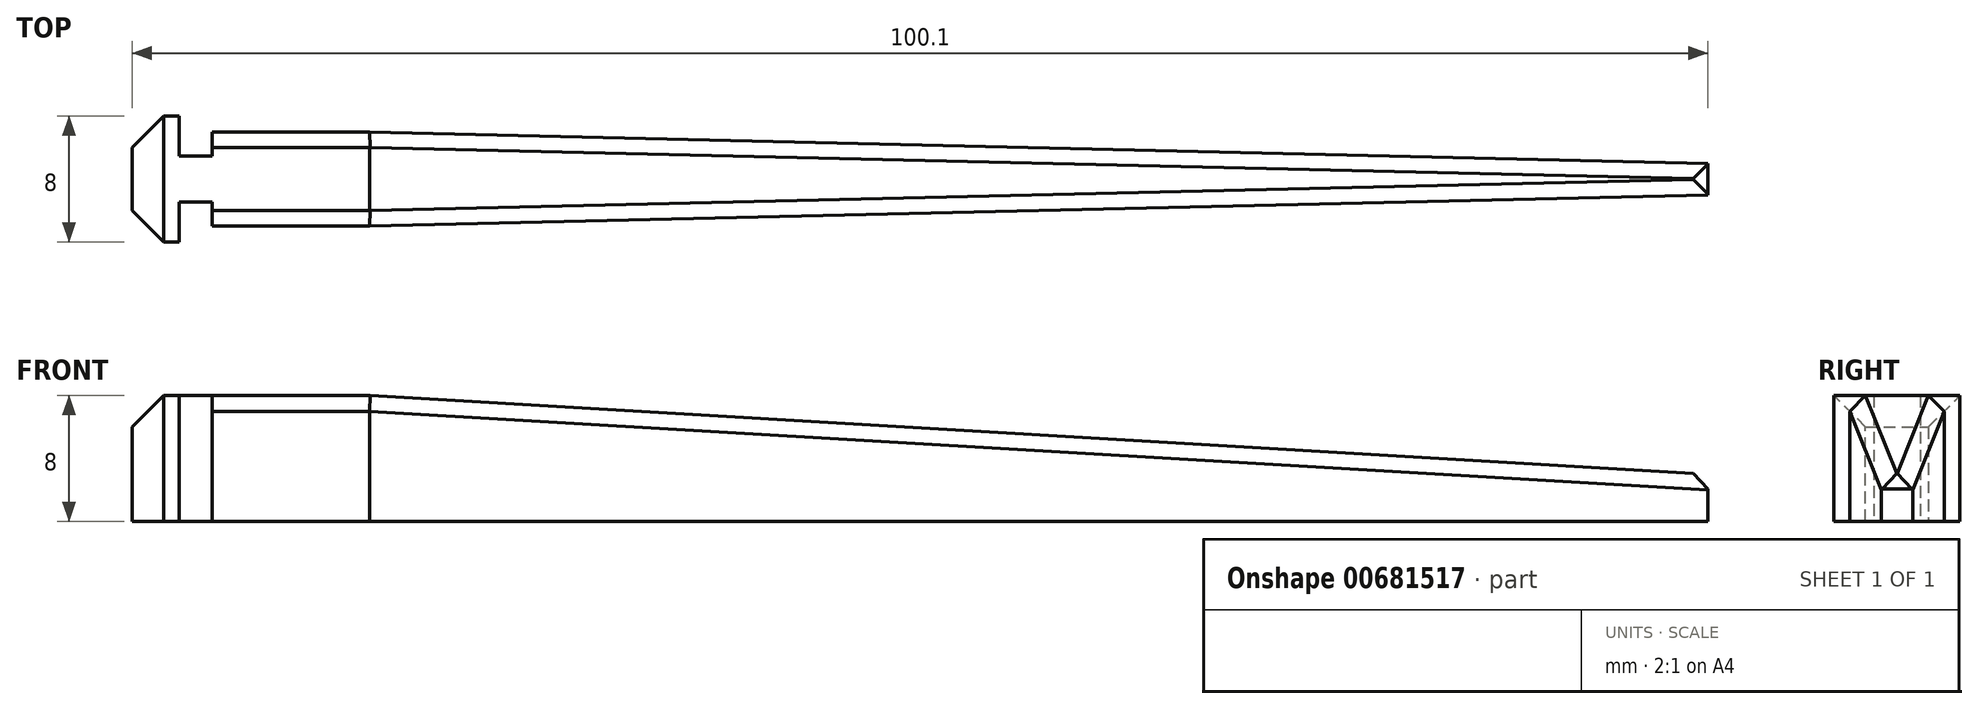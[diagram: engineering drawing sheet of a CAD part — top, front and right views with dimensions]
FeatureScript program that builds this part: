
annotation { "Feature Type Name" : "Feature", "Feature Type Description" : "" }
export const myFeature = defineFeature(function(context is Context, id is Id, definition is map)
    precondition{}
    {
        {
            var Q0;
            Q0=qCreatedBy(makeId("Top.planeOp"),FACE);
            var sketch = newSketch(context, id + "F0", { "sketchPlane" : qUnion([Q0])});
            skLineSegment(sketch, "E0.bottom", {"start": v(0, 0) * mm, "end": v(95, 0) * mm});
            skLineSegment(sketch, "E0.top", {"start": v(0, 6) * mm, "end": v(95, 6) * mm});
            skLineSegment(sketch, "E0.left", {"start": v(0, 0) * mm, "end": v(0, 1.52) * mm});
            skLineSegment(sketch, "E0.right", {"start": v(95, 0) * mm, "end": v(95, 6) * mm});
            skLineSegment(sketch, "E1.bottom", {"start": v(-2.1, 4.47) * mm, "end": v(0, 4.47) * mm});
            skLineSegment(sketch, "E1.top", {"start": v(-2.1, 1.52) * mm, "end": v(0, 1.52) * mm});
            skLineSegment(sketch, "E2.trimOffspring", {"start": v(0, 4.47) * mm, "end": v(0, 6) * mm});
            skLineSegment(sketch, "E3.bottom", {"start": v(-2.1, -1) * mm, "end": v(-5.1, -1) * mm});
            skLineSegment(sketch, "E3.top", {"start": v(-2.1, 7) * mm, "end": v(-5.1, 7) * mm});
            skLineSegment(sketch, "E3.left", {"start": v(-2.1, -1) * mm, "end": v(-2.1, 1.52) * mm});
            skLineSegment(sketch, "E3.right", {"start": v(-5.1, -1) * mm, "end": v(-5.1, 7) * mm});
            skLineSegment(sketch, "E4.trimOffspring", {"start": v(-2.1, 4.47) * mm, "end": v(-2.1, 7) * mm});
            skSolve(sketch);
        }
        {
            var Q0;
            Q0=makeQuery(id+"F0.imprint","IMPRINT",FACE,{"disambiguationData":[TD([[makeQuery(id+"F0.imprint","IMPRINT",EDGE,{"derivedFrom":sQuery(id+"F0.wireOp",EDGE,"E0.bottom")}),1.0]])]});
            extrude(context, id + "F1", {"entities" : qUnion([Q0]), "depth" : 8 * mm, "offsetDistance" : 25 * mm});
        }
        {
            var Q0;
            Q0=makeQuery(id+"F1.opExtrude","SWEPT_EDGE",EDGE,{"disambiguationData":[OSD([sQuery(id+"F0.wireOp",EDGE,"E3.top"),sQuery(id+"F0.wireOp",EDGE,"E3.right")])]});
            var Q1;
            Q1=makeQuery(id+"F1.opExtrude","CAP_EDGE",EDGE,{"disambiguationData":[OSD([sQuery(id+"F0.wireOp",EDGE,"E3.right")])],"isStart":false});
            var Q2;
            Q2=makeQuery(id+"F1.opExtrude","SWEPT_EDGE",EDGE,{"disambiguationData":[OSD([sQuery(id+"F0.wireOp",EDGE,"E3.bottom"),sQuery(id+"F0.wireOp",EDGE,"E3.right")])]});
            chamfer(context, id + "F2", {"entities" : qUnion([Q0, Q1, Q2]), "width" : 2 * mm, "tangentPropagation" : true});
        }
        {
            var Q0;
            Q0=makeQuery(id+"F1.opExtrude","CAP_EDGE",EDGE,{"disambiguationData":[OSD([sQuery(id+"F0.wireOp",EDGE,"E0.right")])],"isStart":false});
            chamfer(context, id + "F3", {"entities" : qUnion([Q0]), "chamferType" : ChamferType.TWO_OFFSETS, "width1" : 85 * mm, "oppositeDirection" : false, "width2" : 5 * mm, "tangentPropagation" : true});
        }
        {
            var Q0;
            Q0=makeQuery(id+"F1.opExtrude","SWEPT_EDGE",EDGE,{"disambiguationData":[OSD([sQuery(id+"F0.wireOp",EDGE,"E0.bottom"),sQuery(id+"F0.wireOp",EDGE,"E0.right")])]});
            var Q1;
            Q1=makeQuery(id+"F1.opExtrude","SWEPT_EDGE",EDGE,{"disambiguationData":[OSD([sQuery(id+"F0.wireOp",EDGE,"E0.top"),sQuery(id+"F0.wireOp",EDGE,"E0.right")])]});
            chamfer(context, id + "F4", {"entities" : qUnion([Q0, Q1]), "chamferType" : ChamferType.TWO_OFFSETS, "width1" : 2 * mm, "oppositeDirection" : false, "width2" : 85 * mm, "tangentPropagation" : true});
        }
        {
            var Q0;
            {var subQ0=sQuery(id+"F0.wireOp",EDGE,"E0.right");Q0=makeQuery(id+"F4.opChamfer","BLEND_EDGE",EDGE,{"blendedFrom":[makeQuery(id+"F1.opExtrude","SWEPT_EDGE",EDGE,{"disambiguationData":[OSD([sQuery(id+"F0.wireOp",EDGE,"E0.bottom"),subQ0])]}),makeQuery(id+"F3.opChamfer","BLEND_FACE",FACE,{"disambiguationData":[OSD([subQ0])]})],"blendedInto":[makeQuery(id+"F3.opChamfer","BLEND_FACE",FACE,{"disambiguationData":[OSD([subQ0])]})]});}
            var Q1;
            {var subQ0=sQuery(id+"F0.wireOp",EDGE,"E0.right");Q1=makeQuery(id+"F4.opChamfer","BLEND_EDGE",EDGE,{"blendedFrom":[makeQuery(id+"F1.opExtrude","SWEPT_EDGE",EDGE,{"disambiguationData":[OSD([sQuery(id+"F0.wireOp",EDGE,"E0.top"),subQ0])]}),makeQuery(id+"F3.opChamfer","BLEND_FACE",FACE,{"disambiguationData":[OSD([subQ0])]})],"blendedInto":[makeQuery(id+"F3.opChamfer","BLEND_FACE",FACE,{"disambiguationData":[OSD([subQ0])]})]});}
            var Q2;
            Q2=makeQuery(id+"F1.opExtrude","CAP_EDGE",EDGE,{"disambiguationData":[OSD([sQuery(id+"F0.wireOp",EDGE,"E0.bottom")])],"isStart":false});
            var Q3;
            Q3=makeQuery(id+"F1.opExtrude","CAP_EDGE",EDGE,{"disambiguationData":[OSD([sQuery(id+"F0.wireOp",EDGE,"E0.top")])],"isStart":false});
            var Q4;
            {var subQ0=sQuery(id+"F0.wireOp",EDGE,"E0.right");Q4=makeQuery(id+"F3.opChamfer","BLEND_EDGE",EDGE,{"blendedFrom":[makeQuery(id+"F1.opExtrude","CAP_EDGE",EDGE,{"disambiguationData":[OSD([subQ0])],"isStart":false}),makeQuery(id+"F1.opExtrude","SWEPT_FACE",FACE,{"disambiguationData":[OSD([subQ0])]})],"blendedInto":[makeQuery(id+"F1.opExtrude","SWEPT_FACE",FACE,{"disambiguationData":[OSD([subQ0])]})]});}
            chamfer(context, id + "F5", {"entities" : qUnion([Q0, Q1, Q2, Q3, Q4]), "width" : 1 * mm, "tangentPropagation" : true});
        }
    });
